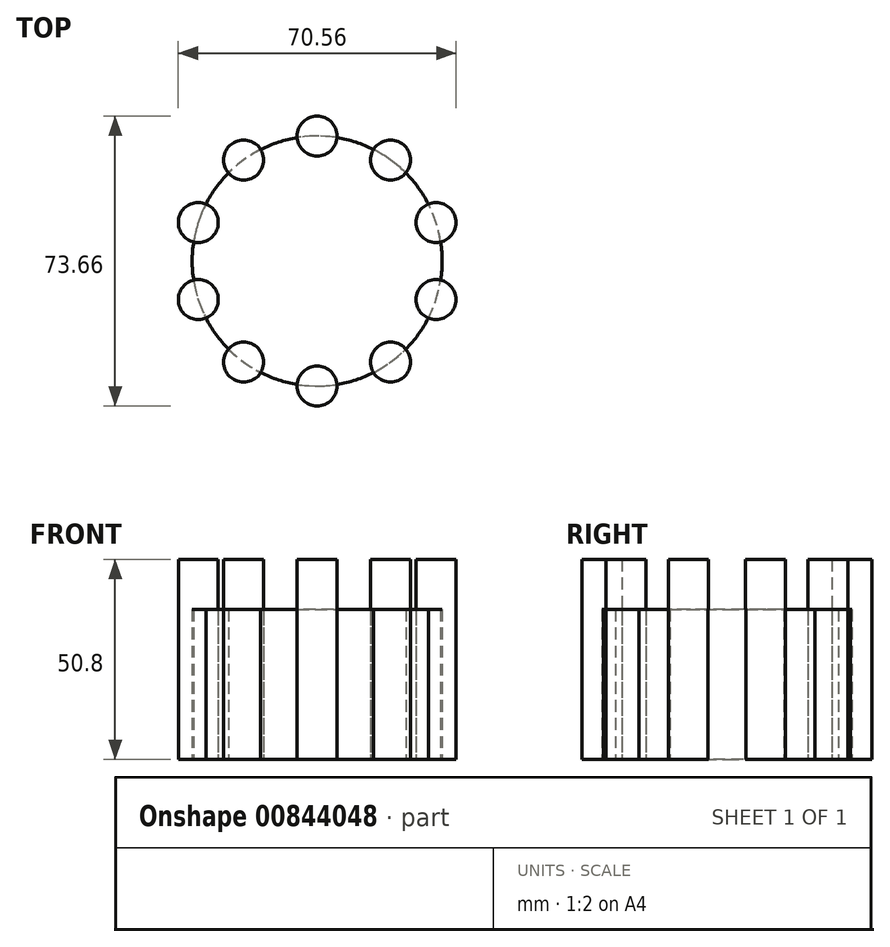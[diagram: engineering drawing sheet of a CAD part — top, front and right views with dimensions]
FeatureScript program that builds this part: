
annotation { "Feature Type Name" : "Feature", "Feature Type Description" : "" }
export const myFeature = defineFeature(function(context is Context, id is Id, definition is map)
    precondition{}
    {
        {
            var Q0;
            Q0=qCreatedBy(makeId("Top.planeOp"),FACE);
            var sketch = newSketch(context, id + "F0", { "sketchPlane" : qUnion([Q0])});
            skCircle(sketch, "E0", {"center": v(0, 0) * mm, "radius": 31.75 * mm});
            skSolve(sketch);
        }
        {
            var Q0;
            Q0=qSketchRegion(id+"F0",true);
            extrude(context, id + "F1", {"entities" : qUnion([Q0]), "depth" : 38.1 * mm});
        }
        {
            var Q0;
            Q0=qCreatedBy(makeId("Top.planeOp"),FACE);
            var sketch = newSketch(context, id + "F2", { "sketchPlane" : qUnion([Q0])});
            skCircle(sketch, "E1", {"center": v(0, 31.75) * mm, "radius": 5.08 * mm});
            skCircle(sketch, "E2.1.0", {"center": v(-18.66, 25.69) * mm, "radius": 5.08 * mm});
            skCircle(sketch, "E2.2.0", {"center": v(-30.2, 9.81) * mm, "radius": 5.08 * mm});
            skCircle(sketch, "E2.3.0", {"center": v(-30.2, -9.81) * mm, "radius": 5.08 * mm});
            skCircle(sketch, "E2.4.0", {"center": v(-18.66, -25.69) * mm, "radius": 5.08 * mm});
            skCircle(sketch, "E2.5.0", {"center": v(0, -31.75) * mm, "radius": 5.08 * mm});
            skCircle(sketch, "E2.6.0", {"center": v(18.66, -25.69) * mm, "radius": 5.08 * mm});
            skCircle(sketch, "E2.7.0", {"center": v(30.2, -9.81) * mm, "radius": 5.08 * mm});
            skCircle(sketch, "E2.8.0", {"center": v(30.2, 9.81) * mm, "radius": 5.08 * mm});
            skCircle(sketch, "E2.9.0", {"center": v(18.66, 25.69) * mm, "radius": 5.08 * mm});
            skPoint(sketch, "E2.center", {"position": v(0, 0) * mm});
            skSolve(sketch);
        }
        {
            var Q0;
            Q0=qSketchRegion(id+"F2",true);
            extrude(context, id + "F3", {"entities" : qUnion([Q0]), "depth" : 50.8 * mm});
        }
        {
            var Q0;
            Q0=makeQuery(id+"F1.opExtrude","SWEPT_BODY",BODY,{"disambiguationData":[OSD([sQuery(id+"F0.wireOp",EDGE,"E0")])]});
            var Q1;
            Q1=makeQuery(id+"F3.opExtrude","SWEPT_BODY",BODY,{"disambiguationData":[OSD([sQuery(id+"F2.wireOp",EDGE,"E2.7.0")])]});
            booleanBodies(context, id + "F4", {"operationType" : BooleanOperationType.INTERSECTION, "tools" : qUnion([Q0, Q1]), "keepTools" : true});
        }
        {
            var Q0;
            Q0=makeQuery(id+"F1.opExtrude","SWEPT_BODY",BODY,{"disambiguationData":[OSD([sQuery(id+"F0.wireOp",EDGE,"E0")])]});
            var Q1;
            Q1=makeQuery(id+"F3.opExtrude","SWEPT_BODY",BODY,{"disambiguationData":[OSD([sQuery(id+"F2.wireOp",EDGE,"E2.6.0")])]});
            booleanBodies(context, id + "F5", {"operationType" : BooleanOperationType.INTERSECTION, "tools" : qUnion([Q0, Q1]), "keepTools" : true});
        }
        {
            var Q0;
            Q0=makeQuery(id+"F1.opExtrude","SWEPT_BODY",BODY,{"disambiguationData":[OSD([sQuery(id+"F0.wireOp",EDGE,"E0")])]});
            var Q1;
            Q1=makeQuery(id+"F3.opExtrude","SWEPT_BODY",BODY,{"disambiguationData":[OSD([sQuery(id+"F2.wireOp",EDGE,"E2.5.0")])]});
            booleanBodies(context, id + "F6", {"operationType" : BooleanOperationType.INTERSECTION, "tools" : qUnion([Q0, Q1]), "keepTools" : true});
        }
        {
            var Q0;
            Q0=makeQuery(id+"F1.opExtrude","SWEPT_BODY",BODY,{"disambiguationData":[OSD([sQuery(id+"F0.wireOp",EDGE,"E0")])]});
            var Q1;
            Q1=makeQuery(id+"F3.opExtrude","SWEPT_BODY",BODY,{"disambiguationData":[OSD([sQuery(id+"F2.wireOp",EDGE,"E2.4.0")])]});
            booleanBodies(context, id + "F7", {"operationType" : BooleanOperationType.INTERSECTION, "tools" : qUnion([Q0, Q1]), "keepTools" : true});
        }
        {
            var Q0;
            Q0=makeQuery(id+"F1.opExtrude","SWEPT_BODY",BODY,{"disambiguationData":[OSD([sQuery(id+"F0.wireOp",EDGE,"E0")])]});
            var Q1;
            Q1=makeQuery(id+"F3.opExtrude","SWEPT_BODY",BODY,{"disambiguationData":[OSD([sQuery(id+"F2.wireOp",EDGE,"E2.3.0")])]});
            booleanBodies(context, id + "F8", {"operationType" : BooleanOperationType.INTERSECTION, "tools" : qUnion([Q0, Q1]), "keepTools" : true});
        }
        {
            var Q0;
            Q0=makeQuery(id+"F3.opExtrude","SWEPT_BODY",BODY,{"disambiguationData":[OSD([sQuery(id+"F2.wireOp",EDGE,"E2.3.0")])]});
            var Q1;
            Q1=makeQuery(id+"F1.opExtrude","SWEPT_BODY",BODY,{"disambiguationData":[OSD([sQuery(id+"F0.wireOp",EDGE,"E0")])]});
            booleanBodies(context, id + "F9", {"operationType" : BooleanOperationType.INTERSECTION, "tools" : qUnion([Q0, Q1]), "keepTools" : true});
        }
        {
            var Q0;
            Q0=makeQuery(id+"F3.opExtrude","SWEPT_BODY",BODY,{"disambiguationData":[OSD([sQuery(id+"F2.wireOp",EDGE,"E2.2.0")])]});
            var Q1;
            Q1=makeQuery(id+"F1.opExtrude","SWEPT_BODY",BODY,{"disambiguationData":[OSD([sQuery(id+"F0.wireOp",EDGE,"E0")])]});
            booleanBodies(context, id + "F10", {"operationType" : BooleanOperationType.INTERSECTION, "tools" : qUnion([Q0, Q1]), "keepTools" : true});
        }
        {
            var Q0;
            Q0=makeQuery(id+"F3.opExtrude","SWEPT_BODY",BODY,{"disambiguationData":[OSD([sQuery(id+"F2.wireOp",EDGE,"E2.1.0")])]});
            var Q1;
            Q1=makeQuery(id+"F1.opExtrude","SWEPT_BODY",BODY,{"disambiguationData":[OSD([sQuery(id+"F0.wireOp",EDGE,"E0")])]});
            booleanBodies(context, id + "F11", {"operationType" : BooleanOperationType.INTERSECTION, "tools" : qUnion([Q0, Q1]), "keepTools" : true});
        }
        {
            var Q0;
            Q0=makeQuery(id+"F3.opExtrude","SWEPT_BODY",BODY,{"disambiguationData":[OSD([sQuery(id+"F2.wireOp",EDGE,"E1")])]});
            var Q1;
            Q1=makeQuery(id+"F1.opExtrude","SWEPT_BODY",BODY,{"disambiguationData":[OSD([sQuery(id+"F0.wireOp",EDGE,"E0")])]});
            booleanBodies(context, id + "F12", {"operationType" : BooleanOperationType.INTERSECTION, "tools" : qUnion([Q0, Q1]), "keepTools" : true});
        }
        {
            var Q0;
            Q0=makeQuery(id+"F3.opExtrude","SWEPT_BODY",BODY,{"disambiguationData":[OSD([sQuery(id+"F2.wireOp",EDGE,"E2.9.0")])]});
            var Q1;
            Q1=makeQuery(id+"F1.opExtrude","SWEPT_BODY",BODY,{"disambiguationData":[OSD([sQuery(id+"F0.wireOp",EDGE,"E0")])]});
            booleanBodies(context, id + "F13", {"operationType" : BooleanOperationType.INTERSECTION, "tools" : qUnion([Q0, Q1]), "keepTools" : true});
        }
        {
            var Q0;
            Q0=makeQuery(id+"F3.opExtrude","SWEPT_BODY",BODY,{"disambiguationData":[OSD([sQuery(id+"F2.wireOp",EDGE,"E2.8.0")])]});
            var Q1;
            Q1=makeQuery(id+"F1.opExtrude","SWEPT_BODY",BODY,{"disambiguationData":[OSD([sQuery(id+"F0.wireOp",EDGE,"E0")])]});
            booleanBodies(context, id + "F14", {"operationType" : BooleanOperationType.INTERSECTION, "tools" : qUnion([Q0, Q1]), "keepTools" : true});
        }
    });
